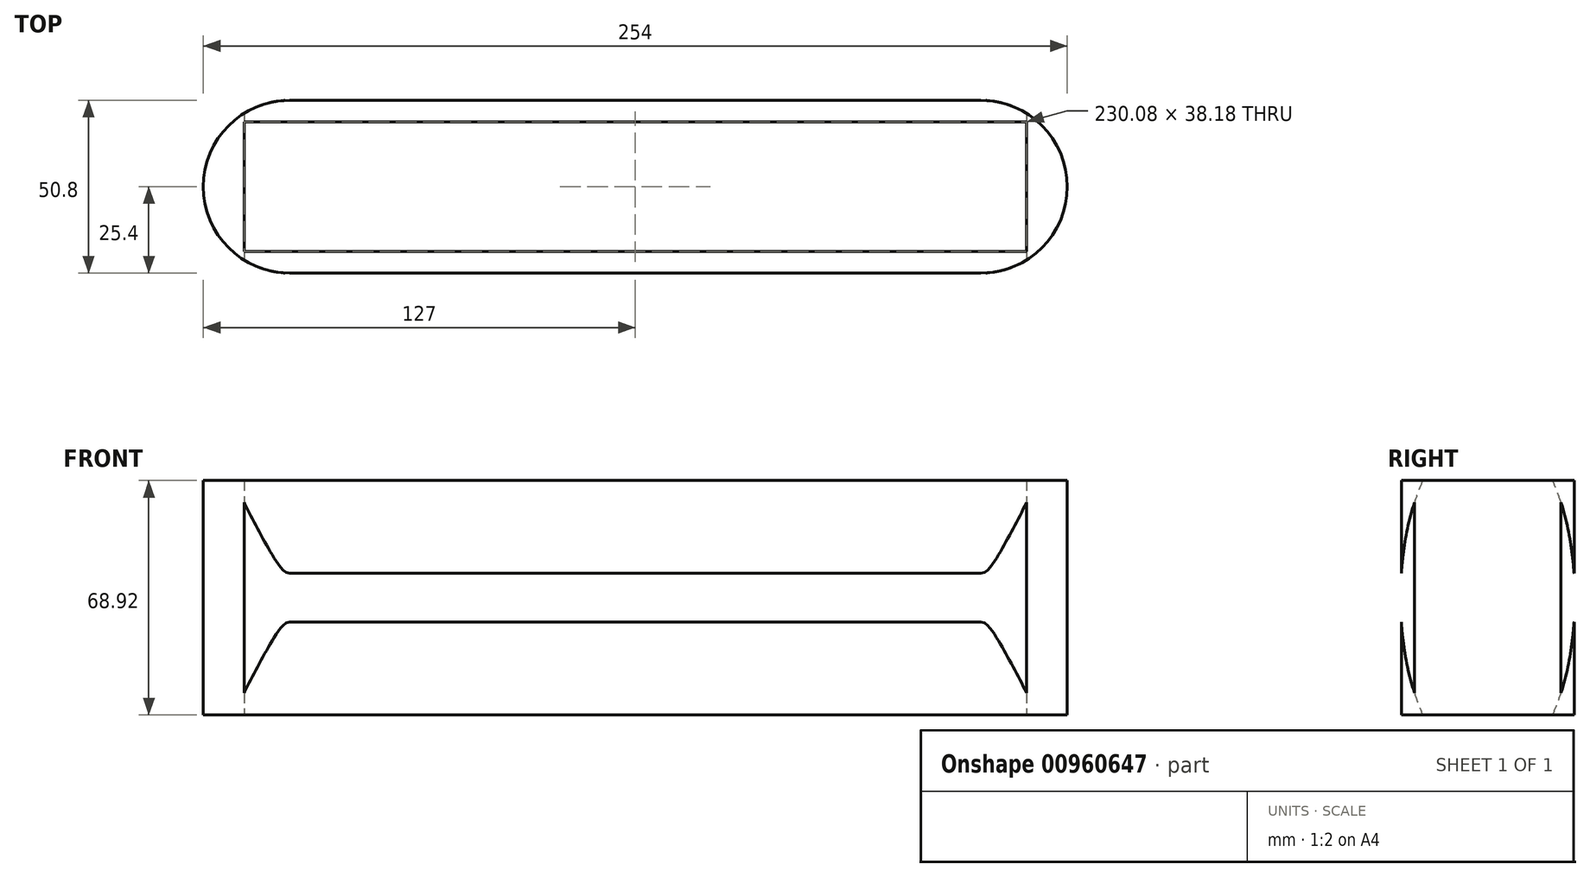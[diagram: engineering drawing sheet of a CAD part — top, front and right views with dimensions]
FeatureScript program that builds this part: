
annotation { "Feature Type Name" : "Feature", "Feature Type Description" : "" }
export const myFeature = defineFeature(function(context is Context, id is Id, definition is map)
    precondition{}
    {
        {
            var Q0;
            Q0=qCreatedBy(makeId("Top.planeOp"),FACE);
            var sketch = newSketch(context, id + "F0", { "sketchPlane" : qUnion([Q0])});
            skLineSegment(sketch, "E0.bottom", {"start": v(101.6, -25.4) * mm, "end": v(-101.6, -25.4) * mm});
            skLineSegment(sketch, "E0.top", {"start": v(101.6, 25.4) * mm, "end": v(-101.6, 25.4) * mm});
            skLineSegment(sketch, "E0.left", {"start": v(101.6, -25.4) * mm, "end": v(101.6, 25.4) * mm});
            skLineSegment(sketch, "E0.right", {"start": v(-101.6, -25.4) * mm, "end": v(-101.6, 25.4) * mm});
            skPoint(sketch, "E0.middle", {"position": v(0, 0) * mm});
            skArc(sketch, "E1", {"start": v(101.6, -25.4) * mm, "mid": v(127, 0) * mm, "end": v(101.6, 25.4) * mm});
            skArc(sketch, "E2", {"start": v(-101.6, 25.4) * mm, "mid": v(-127, 0) * mm, "end": v(-101.6, -25.4) * mm});
            skSolve(sketch);
        }
        {
            var Q0;
            Q0=makeQuery(id+"F0.imprint","IMPRINT",FACE,{"disambiguationData":[TD([[makeQuery(id+"F0.imprint","IMPRINT",EDGE,{"derivedFrom":sQuery(id+"F0.wireOp",EDGE,"E0.bottom")}),-1.0]])]});
            var Q1;
            Q1=makeQuery(id+"F0.imprint","IMPRINT",FACE,{"disambiguationData":[TD([[makeQuery(id+"F0.imprint","IMPRINT",EDGE,{"derivedFrom":sQuery(id+"F0.wireOp",EDGE,"E0.left")}),-1.0]])]});
            var Q2;
            Q2=makeQuery(id+"F0.imprint","IMPRINT",FACE,{"disambiguationData":[TD([[makeQuery(id+"F0.imprint","IMPRINT",EDGE,{"derivedFrom":sQuery(id+"F0.wireOp",EDGE,"E0.right")}),1.0]])]});
            extrude(context, id + "F1", {"entities" : qUnion([Q0, Q1, Q2]), "endBound" : BoundingType.SYMMETRIC, "depth" : 68.92 * mm, "offsetDistance" : 25.4 * mm});
        }
        {
            var Q0;
            Q0=qCreatedBy(makeId("Right.planeOp"),FACE);
            var sketch = newSketch(context, id + "F2", { "sketchPlane" : qUnion([Q0])});
            skLineSegment(sketch, "E3", {"start": v(7.16, 12) * mm, "end": v(-7.16, 12) * mm});
            skLineSegment(sketch, "E4", {"start": v(-7.16, 12) * mm, "end": v(-33.07, 75.2) * mm});
            skLineSegment(sketch, "E5", {"start": v(7.16, 12) * mm, "end": v(33.07, 75.2) * mm});
            skLineSegment(sketch, "E6", {"start": v(33.07, 75.2) * mm, "end": v(-33.07, 75.2) * mm});
            skSolve(sketch);
        }
        {
            var Q0;
            Q0=makeQuery(id+"F2.imprint","IMPRINT",FACE,{"disambiguationData":[TD([[makeQuery(id+"F2.imprint","IMPRINT",EDGE,{"derivedFrom":sQuery(id+"F2.wireOp",EDGE,"E3")}),-1.0]])]});
            extrude(context, id + "F3", {"entities" : qUnion([Q0]), "operationType" : NewBodyOperationType.REMOVE, "endBound" : BoundingType.SYMMETRIC, "oppositeDirection" : true, "depth" : 201.3 * mm, "offsetDistance" : 25.4 * mm});
        }
        {
            var Q0;
            Q0=qCreatedBy(makeId("Right.planeOp"),FACE);
            var sketch = newSketch(context, id + "F4", { "sketchPlane" : qUnion([Q0])});
            skEllipse(sketch, "E7", {"center": v(0, 0) * mm, "majorRadius": 51.61 * mm, "minorRadius": 25.65 * mm, "majorAxis": v(0, -1)});
            skSolve(sketch);
        }
        {
            var Q0;
            Q0=makeQuery(id+"F4.imprint","IMPRINT",FACE,{"disambiguationData":[TD([[makeQuery(id+"F4.imprint","IMPRINT",EDGE,{"derivedFrom":sQuery(id+"F4.wireOp",EDGE,"E7")}),1.0]])]});
            extrude(context, id + "F5", {"entities" : qUnion([Q0]), "operationType" : NewBodyOperationType.REMOVE, "endBound" : BoundingType.SYMMETRIC, "oppositeDirection" : true, "depth" : 230.08 * mm, "offsetDistance" : 25.4 * mm});
        }
    });
